# Revit family: 4405BF
name_source: partatom
category: Plumbing Fixtures
units: mm (PartAtom-declared; Revit-internal decimal feet)

## family parameters
Always vertical = Yes
Cut with Voids When Loaded = No
OmniClass Number = 23.45.00.00
OmniClass Title = Sanitary, Laundry, and Cleaning Equipment
Part Type = Normal
Room Calculation Point = No
Round Connector Dimension = Use Radius
Shared = No
Work Plane-Based = No

## types (2) — shared parameters
Activation = Push Button
Apparent Load Phase 1 = 0 VA
Body Material = Metal - Steel - Painted - Spruce Green
CW Connection = Yes
Chiller Option = No
Cooler Depth = 1' - 7 1/8"
Cooler Width = 0' - 10"
Description = Bottle Filler
Fountain = OUTDOOR
HW Connection = No
Manufacturer = Elkay
Model = LK4405BF
Mounting = Wall Mount
Number of Poles = 1
Rim Height = 2' - 10"
Sanitary Service Size Radius = 0' - 0"
Type = Outdoor
URL = http://www.eklayusa.com
Vent Connection = No
Version = 1.0.0.0
Voltage = 0 V
Volts/Hertz = 115V/60Hz
Wall Plate Material = Metal - Steel - Painted - Spruce Green
Waste Connection = Yes
Water Service Flow = 0 GPM
Water Service Flow Out = 0 GPM
Water Service Radius = 0' - 0"
Water Service Size Radius = 0' - 0 3/16"
zero-valued in all types: Power Factor

## per-type parameters (varying)
| type | Freeze Resistant |
| 4405BF |  |
| 4405BFFR | YES |

## geometry (parser evidence)
native form markers: Sweep x2
no freeform markers — native parametric forms only
